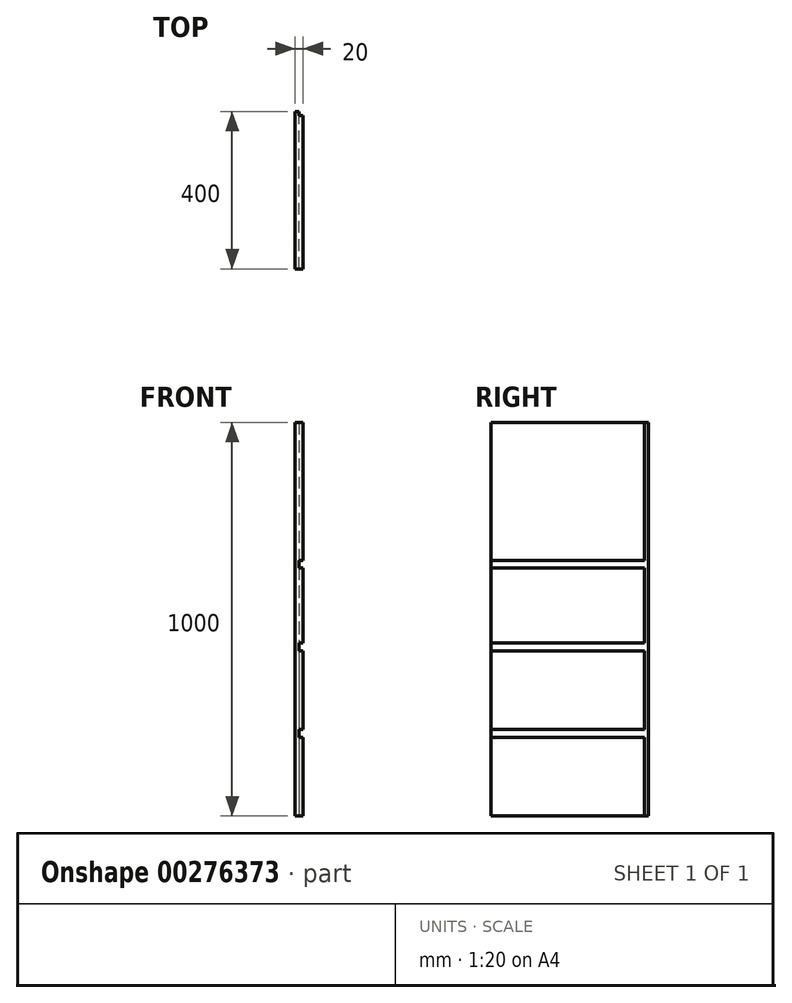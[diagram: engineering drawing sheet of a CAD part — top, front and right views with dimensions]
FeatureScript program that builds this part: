
annotation { "Feature Type Name" : "Feature", "Feature Type Description" : "" }
export const myFeature = defineFeature(function(context is Context, id is Id, definition is map)
    precondition{}
    {
        {
            var Q0;
            Q0=qCreatedBy(makeId("Right.planeOp"),FACE);
            var sketch = newSketch(context, id + "F0", { "sketchPlane" : qUnion([Q0])});
            skLineSegment(sketch, "E0.bottom", {"start": v(-204.88, 686.89) * mm, "end": v(195.12, 686.89) * mm});
            skLineSegment(sketch, "E0.top", {"start": v(-204.88, -313.11) * mm, "end": v(195.12, -313.11) * mm});
            skLineSegment(sketch, "E0.left", {"start": v(-204.88, 686.89) * mm, "end": v(-204.88, -313.11) * mm});
            skLineSegment(sketch, "E0.right", {"start": v(195.12, 686.89) * mm, "end": v(195.12, -313.11) * mm});
            skLineSegment(sketch, "E1", {"start": v(-204.88, -113.11) * mm, "end": v(195.12, -113.11) * mm});
            skLineSegment(sketch, "E2", {"start": v(-204.88, 336.89) * mm, "end": v(195.12, 336.89) * mm});
            skLineSegment(sketch, "E3", {"start": v(-204.88, 316.89) * mm, "end": v(195.12, 316.89) * mm});
            skLineSegment(sketch, "E4", {"start": v(-204.88, 126.89) * mm, "end": v(195.12, 126.89) * mm});
            skLineSegment(sketch, "E5", {"start": v(-204.88, 106.89) * mm, "end": v(195.12, 106.89) * mm});
            skLineSegment(sketch, "E6", {"start": v(-204.88, -93.11) * mm, "end": v(195.12, -93.11) * mm});
            skLineSegment(sketch, "E7", {"start": v(185.12, 686.89) * mm, "end": v(185.12, -313.11) * mm});
            skSolve(sketch);
        }
        {
            var Q0;
            {var subQ0=sQuery(id+"F0.wireOp",EDGE,"E0.right");var subQ1=sQuery(id+"F0.wireOp",EDGE,"E0.bottom");var subQ2=makeQuery(id+"F0.imprint","INTERSECT",VERTEX,{"derivedFrom":[subQ1,subQ0]});Q0=makeQuery(id+"F0.imprint","IMPRINT",FACE,{"disambiguationData":[TD([[makeQuery(id+"F0.imprint","IMPRINT",EDGE,{"disambiguationData":[TD([[subQ2,1.0]])],"derivedFrom":subQ1}),-1.0]])]});}
            var Q1;
            {var subQ0=sQuery(id+"F0.wireOp",EDGE,"E2");var subQ1=sQuery(id+"F0.wireOp",EDGE,"E0.right");var subQ2=makeQuery(id+"F0.imprint","INTERSECT",VERTEX,{"derivedFrom":[subQ1,subQ0]});Q1=makeQuery(id+"F0.imprint","IMPRINT",FACE,{"disambiguationData":[TD([[makeQuery(id+"F0.imprint","IMPRINT",EDGE,{"disambiguationData":[TD([[subQ2,-1.0]])],"derivedFrom":subQ1}),-1.0]])]});}
            var Q2;
            {var subQ0=sQuery(id+"F0.wireOp",EDGE,"E3");var subQ1=sQuery(id+"F0.wireOp",EDGE,"E0.right");var subQ2=makeQuery(id+"F0.imprint","INTERSECT",VERTEX,{"derivedFrom":[subQ1,subQ0]});Q2=makeQuery(id+"F0.imprint","IMPRINT",FACE,{"disambiguationData":[TD([[makeQuery(id+"F0.imprint","IMPRINT",EDGE,{"disambiguationData":[TD([[subQ2,-1.0]])],"derivedFrom":subQ1}),-1.0]])]});}
            var Q3;
            {var subQ0=sQuery(id+"F0.wireOp",EDGE,"E4");var subQ1=sQuery(id+"F0.wireOp",EDGE,"E0.right");var subQ2=makeQuery(id+"F0.imprint","INTERSECT",VERTEX,{"derivedFrom":[subQ1,subQ0]});Q3=makeQuery(id+"F0.imprint","IMPRINT",FACE,{"disambiguationData":[TD([[makeQuery(id+"F0.imprint","IMPRINT",EDGE,{"disambiguationData":[TD([[subQ2,-1.0]])],"derivedFrom":subQ1}),-1.0]])]});}
            var Q4;
            {var subQ0=sQuery(id+"F0.wireOp",EDGE,"E5");var subQ1=sQuery(id+"F0.wireOp",EDGE,"E0.right");var subQ2=makeQuery(id+"F0.imprint","INTERSECT",VERTEX,{"derivedFrom":[subQ1,subQ0]});Q4=makeQuery(id+"F0.imprint","IMPRINT",FACE,{"disambiguationData":[TD([[makeQuery(id+"F0.imprint","IMPRINT",EDGE,{"disambiguationData":[TD([[subQ2,-1.0]])],"derivedFrom":subQ1}),-1.0]])]});}
            var Q5;
            {var subQ0=sQuery(id+"F0.wireOp",EDGE,"E1");var subQ1=sQuery(id+"F0.wireOp",EDGE,"E0.right");var subQ2=makeQuery(id+"F0.imprint","INTERSECT",VERTEX,{"derivedFrom":[subQ1,subQ0]});Q5=makeQuery(id+"F0.imprint","IMPRINT",FACE,{"disambiguationData":[TD([[makeQuery(id+"F0.imprint","IMPRINT",EDGE,{"disambiguationData":[TD([[subQ2,1.0]])],"derivedFrom":subQ1}),-1.0]])]});}
            var Q6;
            {var subQ0=sQuery(id+"F0.wireOp",EDGE,"E0.right");var subQ1=sQuery(id+"F0.wireOp",EDGE,"E0.top");var subQ2=makeQuery(id+"F0.imprint","INTERSECT",VERTEX,{"derivedFrom":[subQ1,subQ0]});Q6=makeQuery(id+"F0.imprint","IMPRINT",FACE,{"disambiguationData":[TD([[makeQuery(id+"F0.imprint","IMPRINT",EDGE,{"disambiguationData":[TD([[subQ2,1.0]])],"derivedFrom":subQ1}),1.0]])]});}
            var Q7;
            {var subQ0=sQuery(id+"F0.wireOp",EDGE,"E1");var subQ1=sQuery(id+"F0.wireOp",EDGE,"E0.left");var subQ2=makeQuery(id+"F0.imprint","INTERSECT",VERTEX,{"derivedFrom":[subQ1,subQ0]});Q7=makeQuery(id+"F0.imprint","IMPRINT",FACE,{"disambiguationData":[TD([[makeQuery(id+"F0.imprint","IMPRINT",EDGE,{"disambiguationData":[TD([[subQ2,1.0]])],"derivedFrom":subQ1}),1.0]])]});}
            var Q8;
            {var subQ0=sQuery(id+"F0.wireOp",EDGE,"E4");var subQ1=sQuery(id+"F0.wireOp",EDGE,"E0.left");var subQ2=makeQuery(id+"F0.imprint","INTERSECT",VERTEX,{"derivedFrom":[subQ1,subQ0]});Q8=makeQuery(id+"F0.imprint","IMPRINT",FACE,{"disambiguationData":[TD([[makeQuery(id+"F0.imprint","IMPRINT",EDGE,{"disambiguationData":[TD([[subQ2,-1.0]])],"derivedFrom":subQ1}),1.0]])]});}
            var Q9;
            {var subQ0=sQuery(id+"F0.wireOp",EDGE,"E2");var subQ1=sQuery(id+"F0.wireOp",EDGE,"E0.left");var subQ2=makeQuery(id+"F0.imprint","INTERSECT",VERTEX,{"derivedFrom":[subQ1,subQ0]});Q9=makeQuery(id+"F0.imprint","IMPRINT",FACE,{"disambiguationData":[TD([[makeQuery(id+"F0.imprint","IMPRINT",EDGE,{"disambiguationData":[TD([[subQ2,-1.0]])],"derivedFrom":subQ1}),1.0]])]});}
            extrude(context, id + "F1", {"entities" : qUnion([Q0, Q1, Q2, Q3, Q4, Q5, Q6, Q7, Q8, Q9]), "depth" : 10 * mm});
        }
        {
            var Q0;
            {var subQ0=sQuery(id+"F0.wireOp",EDGE,"E0.left");var subQ1=sQuery(id+"F0.wireOp",EDGE,"E0.bottom");var subQ2=makeQuery(id+"F0.imprint","INTERSECT",VERTEX,{"derivedFrom":[subQ1,subQ0]});Q0=makeQuery(id+"F0.imprint","IMPRINT",FACE,{"disambiguationData":[TD([[makeQuery(id+"F0.imprint","IMPRINT",EDGE,{"disambiguationData":[TD([[subQ2,-1.0]])],"derivedFrom":subQ1}),-1.0]])]});}
            var Q1;
            {var subQ0=sQuery(id+"F0.wireOp",EDGE,"E3");var subQ1=sQuery(id+"F0.wireOp",EDGE,"E0.left");var subQ2=makeQuery(id+"F0.imprint","INTERSECT",VERTEX,{"derivedFrom":[subQ1,subQ0]});Q1=makeQuery(id+"F0.imprint","IMPRINT",FACE,{"disambiguationData":[TD([[makeQuery(id+"F0.imprint","IMPRINT",EDGE,{"disambiguationData":[TD([[subQ2,-1.0]])],"derivedFrom":subQ1}),1.0]])]});}
            var Q2;
            {var subQ0=sQuery(id+"F0.wireOp",EDGE,"E5");var subQ1=sQuery(id+"F0.wireOp",EDGE,"E0.left");var subQ2=makeQuery(id+"F0.imprint","INTERSECT",VERTEX,{"derivedFrom":[subQ1,subQ0]});Q2=makeQuery(id+"F0.imprint","IMPRINT",FACE,{"disambiguationData":[TD([[makeQuery(id+"F0.imprint","IMPRINT",EDGE,{"disambiguationData":[TD([[subQ2,-1.0]])],"derivedFrom":subQ1}),1.0]])]});}
            var Q3;
            {var subQ0=sQuery(id+"F0.wireOp",EDGE,"E0.left");var subQ1=sQuery(id+"F0.wireOp",EDGE,"E0.top");var subQ2=makeQuery(id+"F0.imprint","INTERSECT",VERTEX,{"derivedFrom":[subQ1,subQ0]});Q3=makeQuery(id+"F0.imprint","IMPRINT",FACE,{"disambiguationData":[TD([[makeQuery(id+"F0.imprint","IMPRINT",EDGE,{"disambiguationData":[TD([[subQ2,-1.0]])],"derivedFrom":subQ1}),1.0]])]});}
            extrude(context, id + "F2", {"entities" : qUnion([Q0, Q1, Q2, Q3]), "operationType" : NewBodyOperationType.ADD, "depth" : 20 * mm});
        }
    });
